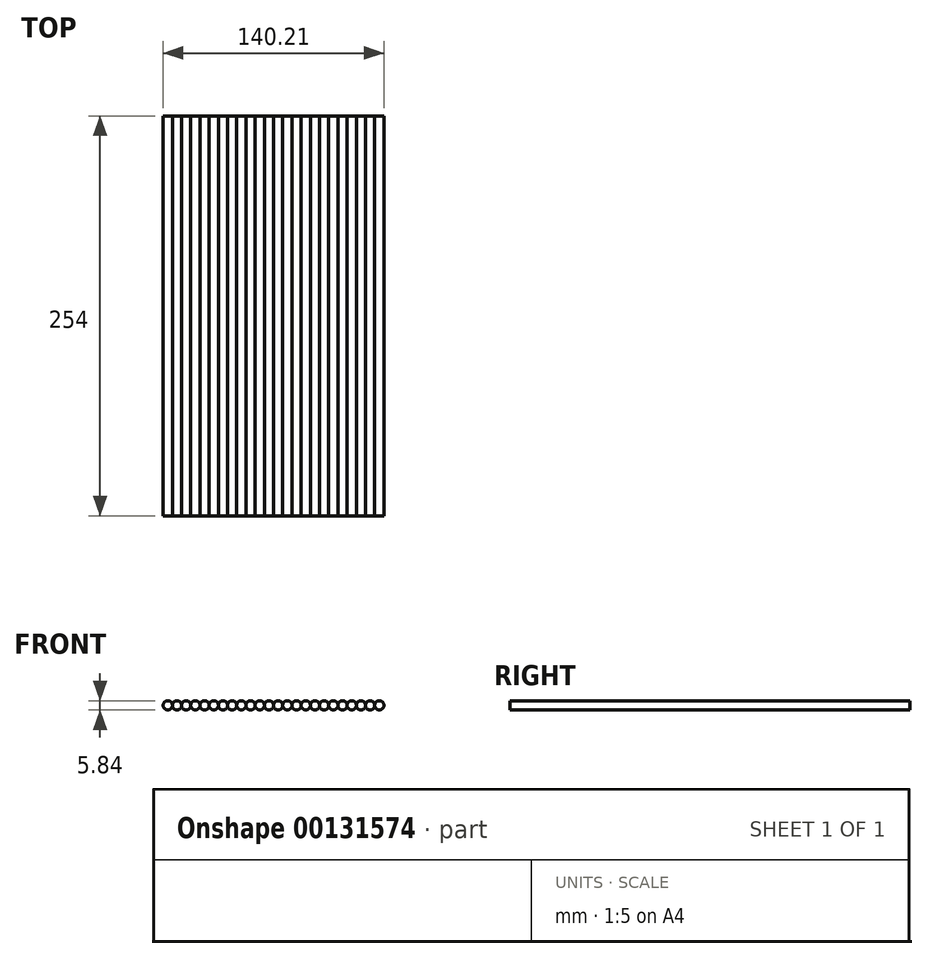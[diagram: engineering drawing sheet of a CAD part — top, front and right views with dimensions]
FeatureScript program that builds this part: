
annotation { "Feature Type Name" : "Feature", "Feature Type Description" : "" }
export const myFeature = defineFeature(function(context is Context, id is Id, definition is map)
    precondition{}
    {
        {
            var Q0;
            Q0=qCreatedBy(makeId("Front.planeOp"),FACE);
            var sketch = newSketch(context, id + "F0", { "sketchPlane" : qUnion([Q0])});
            skCircle(sketch, "E0", {"center": v(0, 0) * mm, "radius": 2.92 * mm});
            skCircle(sketch, "E1", {"center": v(29.21, 0) * mm, "radius": 2.92 * mm});
            skCircle(sketch, "E2", {"center": v(5.84, 0) * mm, "radius": 2.92 * mm});
            skCircle(sketch, "E3", {"center": v(17.53, 0) * mm, "radius": 2.92 * mm});
            skCircle(sketch, "E4", {"center": v(23.37, 0) * mm, "radius": 2.92 * mm});
            skCircle(sketch, "E5", {"center": v(40.9, 0) * mm, "radius": 2.92 * mm});
            skCircle(sketch, "E6", {"center": v(46.74, 0) * mm, "radius": 2.92 * mm});
            skCircle(sketch, "E7", {"center": v(35.05, 0) * mm, "radius": 2.92 * mm});
            skCircle(sketch, "E8", {"center": v(11.68, 0) * mm, "radius": 2.92 * mm});
            skCircle(sketch, "E9", {"center": v(-11.68, 0) * mm, "radius": 2.92 * mm});
            skCircle(sketch, "E10", {"center": v(-17.53, 0) * mm, "radius": 2.92 * mm});
            skCircle(sketch, "E11", {"center": v(-23.37, 0) * mm, "radius": 2.92 * mm});
            skCircle(sketch, "E12", {"center": v(-29.21, 0) * mm, "radius": 2.92 * mm});
            skCircle(sketch, "E13", {"center": v(-35.05, 0) * mm, "radius": 2.92 * mm});
            skCircle(sketch, "E14", {"center": v(-46.74, 0) * mm, "radius": 2.92 * mm});
            skCircle(sketch, "E15", {"center": v(-40.9, 0) * mm, "radius": 2.92 * mm});
            skCircle(sketch, "E16", {"center": v(-5.84, 0) * mm, "radius": 2.92 * mm});
            skCircle(sketch, "E17", {"center": v(-52.58, 0) * mm, "radius": 2.92 * mm});
            skCircle(sketch, "E18", {"center": v(-58.42, 0) * mm, "radius": 2.92 * mm});
            skCircle(sketch, "E19", {"center": v(58.42, 0) * mm, "radius": 2.92 * mm});
            skCircle(sketch, "E20", {"center": v(64.26, 0) * mm, "radius": 2.92 * mm});
            skCircle(sketch, "E21", {"center": v(52.58, 0) * mm, "radius": 2.92 * mm});
            skCircle(sketch, "E22", {"center": v(-64.26, 0) * mm, "radius": 2.92 * mm});
            skCircle(sketch, "E23", {"center": v(70.1, 0) * mm, "radius": 2.92 * mm});
            skSolve(sketch);
        }
        {
            var Q0;
            Q0=makeQuery(id+"F0.imprint","IMPRINT",FACE,{"disambiguationData":[TD([[makeQuery(id+"F0.imprint","IMPRINT",EDGE,{"derivedFrom":sQuery(id+"F0.wireOp",EDGE,"E22")}),1.0]])]});
            var Q1;
            {var subQ0=sQuery(id+"F0.wireOp",EDGE,"E18");var subQ1=makeQuery(id+"F0.imprint","INTERSECT",VERTEX,{"derivedFrom":[subQ0,sQuery(id+"F0.wireOp",EDGE,"E17")]});Q1=makeQuery(id+"F0.imprint","IMPRINT",FACE,{"disambiguationData":[TD([[makeQuery(id+"F0.imprint","IMPRINT",EDGE,{"disambiguationData":[TD([[subQ1,1.0]])],"derivedFrom":subQ0}),1.0]])]});}
            var Q2;
            {var subQ0=sQuery(id+"F0.wireOp",EDGE,"E17");var subQ1=makeQuery(id+"F0.imprint","INTERSECT",VERTEX,{"derivedFrom":[sQuery(id+"F0.wireOp",EDGE,"E18"),subQ0]});Q2=makeQuery(id+"F0.imprint","IMPRINT",FACE,{"disambiguationData":[TD([[makeQuery(id+"F0.imprint","IMPRINT",EDGE,{"disambiguationData":[TD([[subQ1,-1.0]])],"derivedFrom":subQ0}),1.0]])]});}
            var Q3;
            {var subQ0=sQuery(id+"F0.wireOp",EDGE,"E14");var subQ1=makeQuery(id+"F0.imprint","INTERSECT",VERTEX,{"derivedFrom":[sQuery(id+"F0.wireOp",EDGE,"E17"),subQ0]});Q3=makeQuery(id+"F0.imprint","IMPRINT",FACE,{"disambiguationData":[TD([[makeQuery(id+"F0.imprint","IMPRINT",EDGE,{"disambiguationData":[TD([[subQ1,-1.0]])],"derivedFrom":subQ0}),1.0]])]});}
            var Q4;
            {var subQ0=sQuery(id+"F0.wireOp",EDGE,"E15");var subQ1=makeQuery(id+"F0.imprint","INTERSECT",VERTEX,{"derivedFrom":[subQ0,sQuery(id+"F0.wireOp",EDGE,"E14")]});Q4=makeQuery(id+"F0.imprint","IMPRINT",FACE,{"disambiguationData":[TD([[makeQuery(id+"F0.imprint","IMPRINT",EDGE,{"disambiguationData":[TD([[subQ1,1.0]])],"derivedFrom":subQ0}),1.0]])]});}
            var Q5;
            {var subQ0=sQuery(id+"F0.wireOp",EDGE,"E13");var subQ1=makeQuery(id+"F0.imprint","INTERSECT",VERTEX,{"derivedFrom":[sQuery(id+"F0.wireOp",EDGE,"E15"),subQ0]});Q5=makeQuery(id+"F0.imprint","IMPRINT",FACE,{"disambiguationData":[TD([[makeQuery(id+"F0.imprint","IMPRINT",EDGE,{"disambiguationData":[TD([[subQ1,1.0]])],"derivedFrom":subQ0}),1.0]])]});}
            var Q6;
            {var subQ0=sQuery(id+"F0.wireOp",EDGE,"E12");var subQ1=makeQuery(id+"F0.imprint","INTERSECT",VERTEX,{"derivedFrom":[sQuery(id+"F0.wireOp",EDGE,"E11"),subQ0]});Q6=makeQuery(id+"F0.imprint","IMPRINT",FACE,{"disambiguationData":[TD([[makeQuery(id+"F0.imprint","IMPRINT",EDGE,{"disambiguationData":[TD([[subQ1,-1.0]])],"derivedFrom":subQ0}),1.0]])]});}
            var Q7;
            {var subQ0=sQuery(id+"F0.wireOp",EDGE,"E11");var subQ1=makeQuery(id+"F0.imprint","INTERSECT",VERTEX,{"derivedFrom":[sQuery(id+"F0.wireOp",EDGE,"E10"),subQ0]});Q7=makeQuery(id+"F0.imprint","IMPRINT",FACE,{"disambiguationData":[TD([[makeQuery(id+"F0.imprint","IMPRINT",EDGE,{"disambiguationData":[TD([[subQ1,-1.0]])],"derivedFrom":subQ0}),1.0]])]});}
            var Q8;
            {var subQ0=sQuery(id+"F0.wireOp",EDGE,"E10");var subQ1=makeQuery(id+"F0.imprint","INTERSECT",VERTEX,{"derivedFrom":[sQuery(id+"F0.wireOp",EDGE,"E9"),subQ0]});Q8=makeQuery(id+"F0.imprint","IMPRINT",FACE,{"disambiguationData":[TD([[makeQuery(id+"F0.imprint","IMPRINT",EDGE,{"disambiguationData":[TD([[subQ1,1.0]])],"derivedFrom":subQ0}),1.0]])]});}
            var Q9;
            {var subQ0=sQuery(id+"F0.wireOp",EDGE,"E9");var subQ1=makeQuery(id+"F0.imprint","INTERSECT",VERTEX,{"derivedFrom":[subQ0,sQuery(id+"F0.wireOp",EDGE,"E10")]});Q9=makeQuery(id+"F0.imprint","IMPRINT",FACE,{"disambiguationData":[TD([[makeQuery(id+"F0.imprint","IMPRINT",EDGE,{"disambiguationData":[TD([[subQ1,-1.0]])],"derivedFrom":subQ0}),1.0]])]});}
            var Q10;
            {var subQ0=sQuery(id+"F0.wireOp",EDGE,"E16");var subQ1=makeQuery(id+"F0.imprint","INTERSECT",VERTEX,{"derivedFrom":[sQuery(id+"F0.wireOp",EDGE,"E0"),subQ0]});Q10=makeQuery(id+"F0.imprint","IMPRINT",FACE,{"disambiguationData":[TD([[makeQuery(id+"F0.imprint","IMPRINT",EDGE,{"disambiguationData":[TD([[subQ1,-1.0]])],"derivedFrom":subQ0}),1.0]])]});}
            var Q11;
            {var subQ0=sQuery(id+"F0.wireOp",EDGE,"E0");var subQ1=makeQuery(id+"F0.imprint","INTERSECT",VERTEX,{"derivedFrom":[subQ0,sQuery(id+"F0.wireOp",EDGE,"E2")]});Q11=makeQuery(id+"F0.imprint","IMPRINT",FACE,{"disambiguationData":[TD([[makeQuery(id+"F0.imprint","IMPRINT",EDGE,{"disambiguationData":[TD([[subQ1,-1.0]])],"derivedFrom":subQ0}),1.0]])]});}
            var Q12;
            {var subQ0=sQuery(id+"F0.wireOp",EDGE,"E2");var subQ1=makeQuery(id+"F0.imprint","INTERSECT",VERTEX,{"derivedFrom":[sQuery(id+"F0.wireOp",EDGE,"E0"),subQ0]});Q12=makeQuery(id+"F0.imprint","IMPRINT",FACE,{"disambiguationData":[TD([[makeQuery(id+"F0.imprint","IMPRINT",EDGE,{"disambiguationData":[TD([[subQ1,1.0]])],"derivedFrom":subQ0}),1.0]])]});}
            var Q13;
            {var subQ0=sQuery(id+"F0.wireOp",EDGE,"E8");var subQ1=makeQuery(id+"F0.imprint","INTERSECT",VERTEX,{"derivedFrom":[sQuery(id+"F0.wireOp",EDGE,"E2"),subQ0]});Q13=makeQuery(id+"F0.imprint","IMPRINT",FACE,{"disambiguationData":[TD([[makeQuery(id+"F0.imprint","IMPRINT",EDGE,{"disambiguationData":[TD([[subQ1,-1.0]])],"derivedFrom":subQ0}),1.0]])]});}
            var Q14;
            {var subQ0=sQuery(id+"F0.wireOp",EDGE,"E3");var subQ1=makeQuery(id+"F0.imprint","INTERSECT",VERTEX,{"derivedFrom":[subQ0,sQuery(id+"F0.wireOp",EDGE,"E4")]});Q14=makeQuery(id+"F0.imprint","IMPRINT",FACE,{"disambiguationData":[TD([[makeQuery(id+"F0.imprint","IMPRINT",EDGE,{"disambiguationData":[TD([[subQ1,-1.0]])],"derivedFrom":subQ0}),1.0]])]});}
            var Q15;
            {var subQ0=sQuery(id+"F0.wireOp",EDGE,"E4");var subQ1=makeQuery(id+"F0.imprint","INTERSECT",VERTEX,{"derivedFrom":[sQuery(id+"F0.wireOp",EDGE,"E1"),subQ0]});Q15=makeQuery(id+"F0.imprint","IMPRINT",FACE,{"disambiguationData":[TD([[makeQuery(id+"F0.imprint","IMPRINT",EDGE,{"disambiguationData":[TD([[subQ1,1.0]])],"derivedFrom":subQ0}),1.0]])]});}
            var Q16;
            {var subQ0=sQuery(id+"F0.wireOp",EDGE,"E1");var subQ1=makeQuery(id+"F0.imprint","INTERSECT",VERTEX,{"derivedFrom":[subQ0,sQuery(id+"F0.wireOp",EDGE,"E4")]});Q16=makeQuery(id+"F0.imprint","IMPRINT",FACE,{"disambiguationData":[TD([[makeQuery(id+"F0.imprint","IMPRINT",EDGE,{"disambiguationData":[TD([[subQ1,-1.0]])],"derivedFrom":subQ0}),1.0]])]});}
            var Q17;
            {var subQ0=sQuery(id+"F0.wireOp",EDGE,"E7");var subQ1=makeQuery(id+"F0.imprint","INTERSECT",VERTEX,{"derivedFrom":[sQuery(id+"F0.wireOp",EDGE,"E1"),subQ0]});Q17=makeQuery(id+"F0.imprint","IMPRINT",FACE,{"disambiguationData":[TD([[makeQuery(id+"F0.imprint","IMPRINT",EDGE,{"disambiguationData":[TD([[subQ1,1.0]])],"derivedFrom":subQ0}),1.0]])]});}
            var Q18;
            {var subQ0=sQuery(id+"F0.wireOp",EDGE,"E5");var subQ1=makeQuery(id+"F0.imprint","INTERSECT",VERTEX,{"derivedFrom":[subQ0,sQuery(id+"F0.wireOp",EDGE,"E6")]});Q18=makeQuery(id+"F0.imprint","IMPRINT",FACE,{"disambiguationData":[TD([[makeQuery(id+"F0.imprint","IMPRINT",EDGE,{"disambiguationData":[TD([[subQ1,-1.0]])],"derivedFrom":subQ0}),1.0]])]});}
            var Q19;
            {var subQ0=sQuery(id+"F0.wireOp",EDGE,"E6");var subQ1=makeQuery(id+"F0.imprint","INTERSECT",VERTEX,{"derivedFrom":[sQuery(id+"F0.wireOp",EDGE,"E5"),subQ0]});Q19=makeQuery(id+"F0.imprint","IMPRINT",FACE,{"disambiguationData":[TD([[makeQuery(id+"F0.imprint","IMPRINT",EDGE,{"disambiguationData":[TD([[subQ1,1.0]])],"derivedFrom":subQ0}),1.0]])]});}
            var Q20;
            {var subQ0=sQuery(id+"F0.wireOp",EDGE,"E21");var subQ1=makeQuery(id+"F0.imprint","INTERSECT",VERTEX,{"derivedFrom":[sQuery(id+"F0.wireOp",EDGE,"E6"),subQ0]});Q20=makeQuery(id+"F0.imprint","IMPRINT",FACE,{"disambiguationData":[TD([[makeQuery(id+"F0.imprint","IMPRINT",EDGE,{"disambiguationData":[TD([[subQ1,-1.0]])],"derivedFrom":subQ0}),1.0]])]});}
            var Q21;
            {var subQ0=sQuery(id+"F0.wireOp",EDGE,"E19");var subQ1=makeQuery(id+"F0.imprint","INTERSECT",VERTEX,{"derivedFrom":[sQuery(id+"F0.wireOp",EDGE,"E20"),subQ0]});Q21=makeQuery(id+"F0.imprint","IMPRINT",FACE,{"disambiguationData":[TD([[makeQuery(id+"F0.imprint","IMPRINT",EDGE,{"disambiguationData":[TD([[subQ1,-1.0]])],"derivedFrom":subQ0}),1.0]])]});}
            var Q22;
            {var subQ0=sQuery(id+"F0.wireOp",EDGE,"E20");var subQ1=makeQuery(id+"F0.imprint","INTERSECT",VERTEX,{"derivedFrom":[subQ0,sQuery(id+"F0.wireOp",EDGE,"E19")]});Q22=makeQuery(id+"F0.imprint","IMPRINT",FACE,{"disambiguationData":[TD([[makeQuery(id+"F0.imprint","IMPRINT",EDGE,{"disambiguationData":[TD([[subQ1,1.0]])],"derivedFrom":subQ0}),1.0]])]});}
            var Q23;
            Q23=makeQuery(id+"F0.imprint","IMPRINT",FACE,{"disambiguationData":[TD([[makeQuery(id+"F0.imprint","IMPRINT",EDGE,{"derivedFrom":sQuery(id+"F0.wireOp",EDGE,"E23")}),1.0]])]});
            extrude(context, id + "F1", {"entities" : qUnion([Q0, Q1, Q2, Q3, Q4, Q5, Q6, Q7, Q8, Q9, Q10, Q11, Q12, Q13, Q14, Q15, Q16, Q17, Q18, Q19, Q20, Q21, Q22, Q23]), "depth" : 254 * mm});
        }
    });
